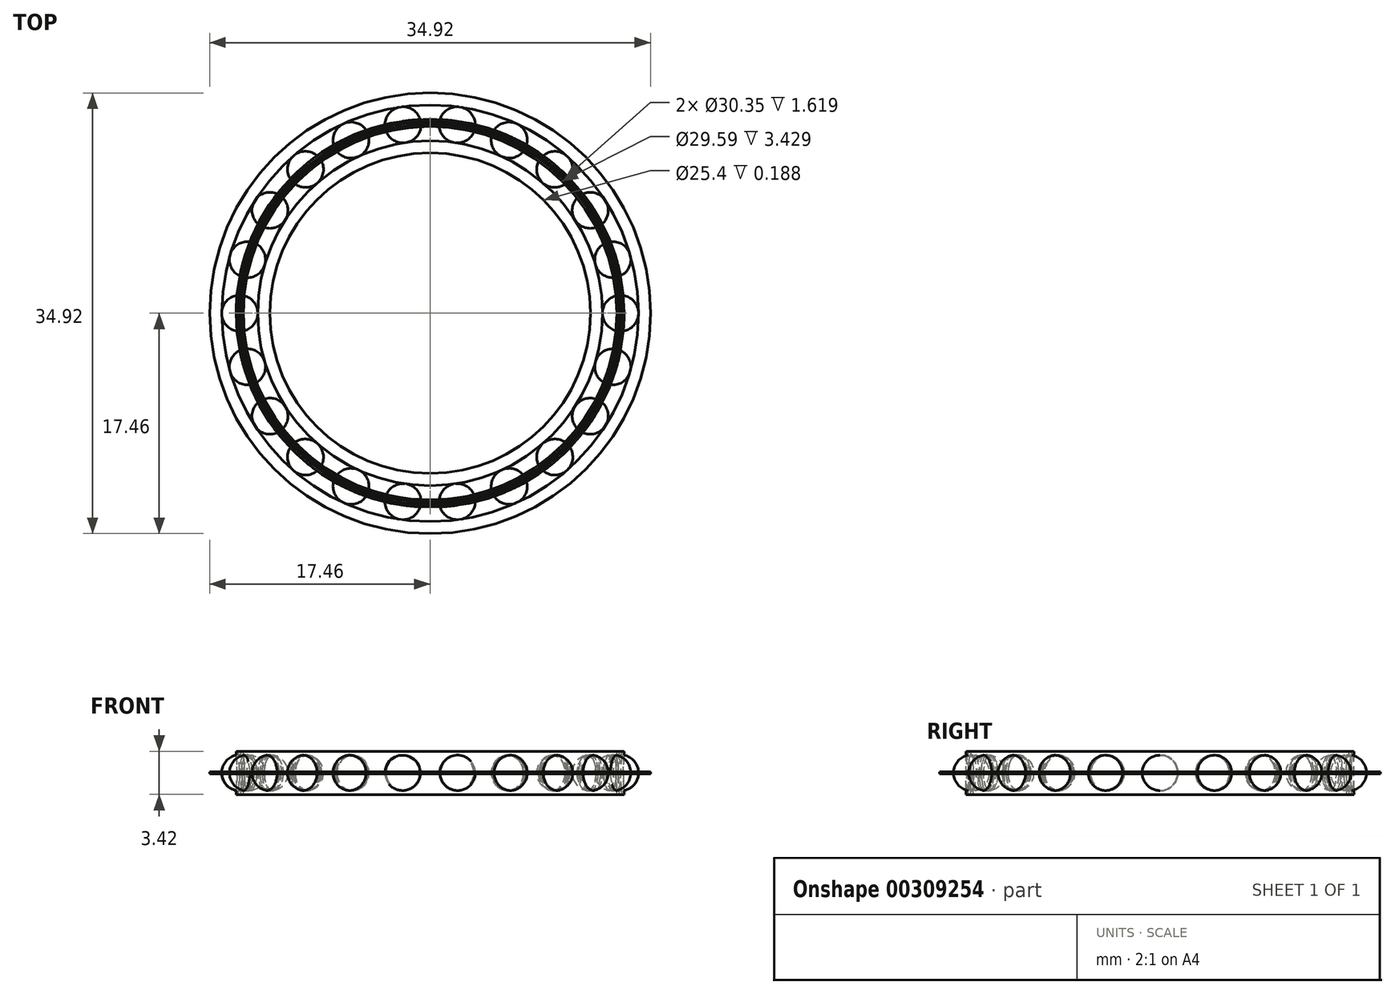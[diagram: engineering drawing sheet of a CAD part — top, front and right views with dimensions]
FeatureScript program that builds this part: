
annotation { "Feature Type Name" : "Feature", "Feature Type Description" : "" }
export const myFeature = defineFeature(function(context is Context, id is Id, definition is map)
    precondition{}
    {
        {
            assignVariable(context, id + "F0", {"name" : "ball_count", "anyValue" : 0});
        }
        {
            assignVariable(context, id + "F1", {"name" : "id_in", "anyValue" : 1});
        }
        {
            assignVariable(context, id + "F2", {"name" : "od_in", "anyValue" : 1.38});
        }
        {
            assignVariable(context, id + "F3", {"name" : "len_in", "anyValue" : 3 / 16});
        }
        {
            assignVariable(context, id + "F4", {"name" : "bMetric", "anyValue" : 0});
        }
        {
            assignVariable(context, id + "F5", {"name" : "id_mm", "anyValue" : 25.4});
        }
        {
            assignVariable(context, id + "F6", {"name" : "od_mm", "anyValue" : 50.8});
        }
        {
            assignVariable(context, id + "F7", {"name" : "len_mm", "anyValue" : 12.7});
        }
        {
            assignVariable(context, id + "F8", {"name" : "id", "anyValue" : [getVariable(context, 'id_in'), getVariable(context, 'id_mm') / 25.4][getVariable(context, 'bMetric')]});
        }
        {
            assignVariable(context, id + "F9", {"name" : "od", "anyValue" : [getVariable(context, 'od_in'), getVariable(context, 'od_mm') / 25.4][getVariable(context, 'bMetric')]});
        }
        {
            assignVariable(context, id + "F10", {"name" : "len", "anyValue" : [getVariable(context, 'len_in'), getVariable(context, 'len_mm') / 25.4][getVariable(context, 'bMetric')]});
        }
        {
            assignVariable(context, id + "F11", {"name" : "radial_thk", "anyValue" : (getVariable(context, 'od') - getVariable(context, 'id')) / 2});
        }
        {
            assignVariable(context, id + "F12", {"name" : "ball_dia", "anyValue" : .6 * getVariable(context, 'radial_thk')});
        }
        {
            assignVariable(context, id + "F13", {"name" : "mean_dia", "anyValue" : (getVariable(context, 'od') + getVariable(context, 'id')) / 2});
        }
        {
            assignVariable(context, id + "F14", {"name" : "ball_calc", "anyValue" : ((PI * getVariable(context, 'mean_dia')) / (1.5 * getVariable(context, 'ball_dia')))});
        }
        {
            assignVariable(context, id + "F15", {"name" : "N", "anyValue" : [floor(getVariable(context, 'ball_calc')), getVariable(context, 'ball_count')][getVariable(context, 'ball_count') % (getVariable(context, 'ball_count') - 1)]});
        }
        {
            var Q0;
            Q0=qCreatedBy(makeId("Top.planeOp"),FACE);
            var sketch = newSketch(context, id + "F16", { "sketchPlane" : qUnion([Q0])});
            skCircle(sketch, "E0", {"center": v(0, 0) * mm, "radius": 12.7 * mm});
            skCircle(sketch, "E1", {"center": v(0, 0) * mm, "radius": 17.46 * mm});
            skSolve(sketch);
        }
        {
            var Q0;
            Q0=qSketchRegion(id+"F16",true);
            extrude(context, id + "F17", {"entities" : qUnion([Q0]), "depth" : (getVariable(context, 'len')) * mm, "symmetric" : true});
        }
        {
            var Q0;
            Q0=qCreatedBy(makeId("Top.planeOp"),FACE);
            var sketch = newSketch(context, id + "F18", { "sketchPlane" : qUnion([Q0])});
            skCircle(sketch, "E2", {"center": v(0, 0) * mm, "radius": 12.7 * mm});
            skCircle(sketch, "E3", {"center": v(0, 0) * mm, "radius": 14.22 * mm});
            skCircle(sketch, "E4", {"center": v(0, 0) * mm, "radius": 15.94 * mm});
            skCircle(sketch, "E5", {"center": v(0, 0) * mm, "radius": 17.46 * mm});
            skCircle(sketch, "E6", {"center": v(0, 0) * mm, "radius": 15.08 * mm, "construction": true});
            skLineSegment(sketch, "E7", {"start": v(14.22, 0) * mm, "end": v(15.94, 0) * mm, "construction": true});
            skPoint(sketch, "E8", {"position": v(15.08, 0) * mm});
            skLineSegment(sketch, "E9", {"start": v(-17.46, 0) * mm, "end": v(-12.7, 0) * mm, "construction": true});
            skPoint(sketch, "E10", {"position": v(-15.08, 0) * mm});
            skPoint(sketch, "E11", {"position": v(12.7, 0) * mm});
            skPoint(sketch, "E12", {"position": v(17.46, 0) * mm});
            skSolve(sketch);
        }
        {
            var Q0;
            Q0=makeQuery(id+"F18.imprint","IMPRINT",FACE,{"disambiguationData":[TD([[makeQuery(id+"F18.imprint","IMPRINT",EDGE,{"derivedFrom":sQuery(id+"F18.wireOp",EDGE,"E4")}),-1.0]])]});
            var Q1;
            Q1=makeQuery(id+"F18.imprint","IMPRINT",FACE,{"disambiguationData":[TD([[makeQuery(id+"F18.imprint","IMPRINT",EDGE,{"derivedFrom":sQuery(id+"F18.wireOp",EDGE,"E2")}),-1.0]])]});
            extrude(context, id + "F19", {"entities" : qUnion([Q0, Q1]), "depth" : (getVariable(context, 'len')) * mm, "symmetric" : true});
        }
        {
            var Q0;
            Q0=makeQuery(id+"F19.opExtrude","CAP_EDGE",EDGE,{"disambiguationData":[OSD([sQuery(id+"F18.wireOp",EDGE,"E5")])],"isStart":false});
            var Q1;
            Q1=makeQuery(id+"F19.opExtrude","CAP_EDGE",EDGE,{"disambiguationData":[OSD([sQuery(id+"F18.wireOp",EDGE,"E5")])],"isStart":true});
            fillet(context, id + "F20", {"entities" : qUnion([Q0, Q1]), "radius" : (getVariable(context, 'len') / 10) * mm, "tangentPropagation" : true, "allowEdgeOverflow" : false});
        }
        {
            var Q0;
            Q0=makeQuery(id+"F19.opExtrude","CAP_EDGE",EDGE,{"disambiguationData":[OSD([sQuery(id+"F18.wireOp",EDGE,"E2")])],"isStart":true});
            var Q1;
            Q1=makeQuery(id+"F19.opExtrude","CAP_EDGE",EDGE,{"disambiguationData":[OSD([sQuery(id+"F18.wireOp",EDGE,"E2")])],"isStart":false});
            fillet(context, id + "F21", {"entities" : qUnion([Q0, Q1]), "radius" : (getVariable(context, 'len') / 15) * mm, "tangentPropagation" : true, "allowEdgeOverflow" : false});
        }
        {
            var Q0;
            Q0=qCreatedBy(makeId("Front.planeOp"),FACE);
            var sketch = newSketch(context, id + "F22", { "sketchPlane" : qUnion([Q0])});
            skLineSegment(sketch, "E13", {"start": v(0, 2.38) * mm, "end": v(0, -2.38) * mm, "construction": true});
            skCircle(sketch, "E14", {"center": v(15.08, 0) * mm, "radius": 1.43 * mm});
            skSolve(sketch);
        }
        {
            var Q0;
            Q0=qSketchRegion(id+"F22",true);
            var Q1;
            Q1=sQuery(id+"F22.wireOp",EDGE,"E13");
            revolve(context, id + "F23", {"operationType" : NewBodyOperationType.REMOVE, "entities" : qUnion([Q0]), "axis" : qUnion([Q1]), "revolveType" : RevolveType.FULL, "oppositeDirection" : true});
        }
        {
            var Q0;
            Q0=qCreatedBy(makeId("Front.planeOp"),FACE);
            var sketch = newSketch(context, id + "F24", { "sketchPlane" : qUnion([Q0])});
            skLineSegment(sketch, "E15.bottom", {"start": v(14.99, -1.71) * mm, "end": v(14.8, -1.71) * mm});
            skLineSegment(sketch, "E15.top", {"start": v(14.99, 1.71) * mm, "end": v(14.8, 1.71) * mm});
            skLineSegment(sketch, "E15.left", {"start": v(14.99, -1.71) * mm, "end": v(14.99, -0.1) * mm});
            skLineSegment(sketch, "E15.right", {"start": v(14.8, -1.71) * mm, "end": v(14.8, 1.71) * mm});
            skLineSegment(sketch, "E16.bottom", {"start": v(15.18, 1.71) * mm, "end": v(15.37, 1.71) * mm});
            skLineSegment(sketch, "E16.top", {"start": v(15.18, -1.71) * mm, "end": v(15.37, -1.71) * mm});
            skLineSegment(sketch, "E16.left", {"start": v(15.18, 1.71) * mm, "end": v(15.18, 0.1) * mm});
            skLineSegment(sketch, "E16.right", {"start": v(15.37, 1.71) * mm, "end": v(15.37, -1.71) * mm});
            skLineSegment(sketch, "E17.bottom", {"start": v(15.18, -0.1) * mm, "end": v(14.99, -0.1) * mm});
            skLineSegment(sketch, "E17.top", {"start": v(15.18, 0.1) * mm, "end": v(14.99, 0.1) * mm});
            skPoint(sketch, "E17.middle", {"position": v(15.08, 0) * mm});
            skLineSegment(sketch, "E18.trimOffspring", {"start": v(14.99, 0.1) * mm, "end": v(14.99, 1.71) * mm});
            skLineSegment(sketch, "E19.trimOffspring", {"start": v(15.18, -0.1) * mm, "end": v(15.18, -1.71) * mm});
            skLineSegment(sketch, "E20", {"start": v(15.08, 0.1) * mm, "end": v(15.08, -0.1) * mm, "construction": true});
            skLineSegment(sketch, "E21", {"start": v(14.99, 0.1) * mm, "end": v(15.18, -0.1) * mm, "construction": true});
            skLineSegment(sketch, "E22", {"start": v(15.18, 0.1) * mm, "end": v(14.99, -0.1) * mm, "construction": true});
            skSolve(sketch);
        }
        {
            var Q0;
            Q0=qSketchRegion(id+"F24",true);
            var Q1;
            Q1=sQuery(id+"F22.wireOp",EDGE,"E13");
            revolve(context, id + "F25", {"entities" : qUnion([Q0]), "axis" : qUnion([Q1]), "revolveType" : RevolveType.FULL});
        }
        {
            var Q0;
            Q0=qCreatedBy(makeId("Front.planeOp"),FACE);
            var sketch = newSketch(context, id + "F26", { "sketchPlane" : qUnion([Q0])});
            skLineSegment(sketch, "E23", {"start": v(-2.38, 0) * mm, "end": v(2.38, 0) * mm, "construction": true});
            skLineSegment(sketch, "E24.0", {"start": v(13.65, 0) * mm, "end": v(13.65, 0) * mm});
            skArc(sketch, "E25", {"start": v(16.51, 0) * mm, "mid": v(15.08, 1.43) * mm, "end": v(13.65, 0) * mm});
            skLineSegment(sketch, "E26", {"start": v(13.65, 0) * mm, "end": v(16.5, 0) * mm});
            skSolve(sketch);
        }
        {
            var Q0;
            Q0=qSketchRegion(id+"F26",true);
            var Q1;
            Q1=sQuery(id+"F26.wireOp",EDGE,"E26");
            revolve(context, id + "F27", {"entities" : qUnion([Q0]), "axis" : qUnion([Q1]), "revolveType" : RevolveType.FULL});
        }
        {
            var Q0;
            Q0=makeQuery(id+"F27.opRevolve","SWEPT_BODY",BODY,{"disambiguationData":[OSD([sQuery(id+"F26.wireOp",EDGE,"E25"),sQuery(id+"F26.wireOp",EDGE,"E26")])]});
            var Q1;
            Q1=makeQuery(id+"F25.opRevolve","SWEPT_FACE",FACE,{"disambiguationData":[OSD([sQuery(id+"F24.wireOp",EDGE,"E15.right")])]});
            circularPattern(context, id + "F28", {"operationType" : NewBodyOperationType.ADD, "entities" : qUnion([Q0]), "axis" : qUnion([Q1]), "angle" : 360 * degree, "instanceCount" : getVariable(context, 'N'), "equalSpace" : true});
        }
    });
